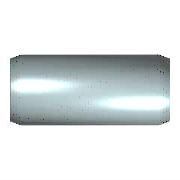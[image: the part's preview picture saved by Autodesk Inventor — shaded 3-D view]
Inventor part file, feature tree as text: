
AUTODESK INVENTOR PART (.ipt)
format: ipt  version: 2023.3 (Build 273359000, 359)  size: 115,712 bytes
history: native  units: mm (DEFAULTED — no unit token found)
features: extrude x1, chamfer x1, sketch x1
ambient origin geometry x8: Origin, YZ Plane, XZ Plane, XY Plane, X Axis, Y Axis, Z Axis, Center Point
bodies: Solid1 (feature_tree)
feature tree (3):
  extrude  "Körper"  Depth=10.0mm
  chamfer  "Skizze2"  [1 undecoded]
  sketch  "Skizze"  dims[d1=3.0mm d2=10.0mm d3=0.0mm d4=0.5mm d5=15.0deg d8=0.5mm d9=15.0deg d11=0.5mm d12=0.5mm d13=0.0mm d15=0.0mm d16=0.0mm]
note: 1 required parameter value undecoded (feature->parameter linkage not recoverable at this tier; creation-order binding heuristic only, values carry confidence <= 0.55)
